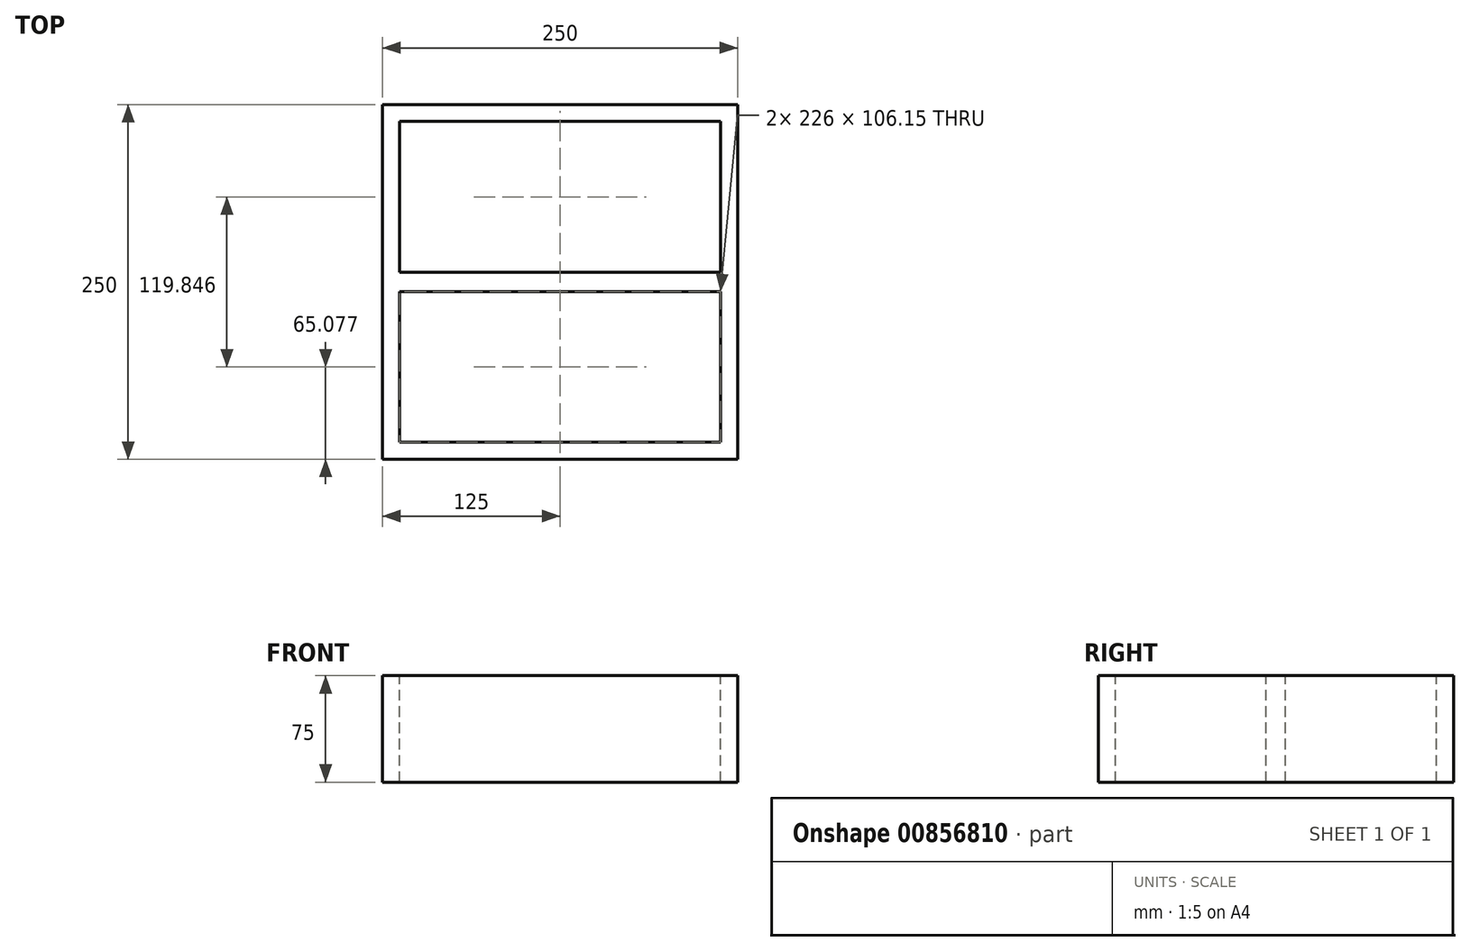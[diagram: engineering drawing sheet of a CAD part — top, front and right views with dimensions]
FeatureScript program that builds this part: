
annotation { "Feature Type Name" : "Feature", "Feature Type Description" : "" }
export const myFeature = defineFeature(function(context is Context, id is Id, definition is map)
    precondition{}
    {
        {
            var Q0;
            Q0=qCreatedBy(makeId("Top.planeOp"),FACE);
            var sketch = newSketch(context, id + "F0", { "sketchPlane" : qUnion([Q0])});
            skLineSegment(sketch, "E0.bottom", {"start": v(-125, 125) * mm, "end": v(125, 125) * mm});
            skLineSegment(sketch, "E0.top", {"start": v(-125, -125) * mm, "end": v(125, -125) * mm});
            skLineSegment(sketch, "E0.left", {"start": v(-125, 125) * mm, "end": v(-125, -125) * mm});
            skLineSegment(sketch, "E0.right", {"start": v(125, 125) * mm, "end": v(125, -125) * mm});
            skPoint(sketch, "E0.middle", {"position": v(0, 0) * mm});
            skSolve(sketch);
        }
        {
            var Q0;
            Q0=makeQuery(id+"F0.imprint","IMPRINT",FACE,{"disambiguationData":[TD([[makeQuery(id+"F0.imprint","IMPRINT",EDGE,{"derivedFrom":sQuery(id+"F0.wireOp",EDGE,"E0.bottom")}),-1.0]])]});
            extrude(context, id + "F1", {"entities" : qUnion([Q0]), "depth" : 75 * mm, "offsetDistance" : 25.4 * mm});
        }
        {
            var Q0;
            Q0=makeQuery(id+"F1.opExtrude","CAP_FACE",FACE,{"disambiguationData":[OSD([sQuery(id+"F0.wireOp",EDGE,"E0.bottom"),sQuery(id+"F0.wireOp",EDGE,"E0.top"),sQuery(id+"F0.wireOp",EDGE,"E0.left"),sQuery(id+"F0.wireOp",EDGE,"E0.right")])],"isStart":false});
            var sketch = newSketch(context, id + "F2", { "sketchPlane" : qUnion([Q0])});
            skLineSegment(sketch, "E1.bottom", {"start": v(-113, 113) * mm, "end": v(113, 113) * mm});
            skLineSegment(sketch, "E1.top", {"start": v(-113, -113) * mm, "end": v(113, -113) * mm});
            skLineSegment(sketch, "E1.left", {"start": v(-113, 113) * mm, "end": v(-113, -113) * mm});
            skLineSegment(sketch, "E1.right", {"start": v(113, 113) * mm, "end": v(113, -113) * mm});
            skPoint(sketch, "E1.middle", {"position": v(0, 0) * mm});
            skSolve(sketch);
        }
        {
            var Q0;
            Q0=makeQuery(id+"F2.imprint","IMPRINT",FACE,{"disambiguationData":[TD([[makeQuery(id+"F2.imprint","IMPRINT",EDGE,{"derivedFrom":sQuery(id+"F2.wireOp",EDGE,"E1.bottom")}),-1.0]])]});
            extrude(context, id + "F3", {"entities" : qUnion([Q0]), "operationType" : NewBodyOperationType.REMOVE, "oppositeDirection" : true, "depth" : 101.6 * mm, "offsetDistance" : 25.4 * mm});
        }
        {
            var Q0;
            Q0=makeQuery(id+"F1.opExtrude","CAP_FACE",FACE,{"disambiguationData":[OSD([sQuery(id+"F0.wireOp",EDGE,"E0.bottom"),sQuery(id+"F0.wireOp",EDGE,"E0.top"),sQuery(id+"F0.wireOp",EDGE,"E0.left"),sQuery(id+"F0.wireOp",EDGE,"E0.right")])],"isStart":false});
            var sketch = newSketch(context, id + "F4", { "sketchPlane" : qUnion([Q0])});
            skLineSegment(sketch, "E2.bottom", {"start": v(-113, 6.85) * mm, "end": v(113, 6.85) * mm});
            skLineSegment(sketch, "E2.top", {"start": v(-113, -6.85) * mm, "end": v(113, -6.85) * mm});
            skLineSegment(sketch, "E2.left", {"start": v(-113, 6.85) * mm, "end": v(-113, -6.85) * mm});
            skLineSegment(sketch, "E2.right", {"start": v(113, 6.85) * mm, "end": v(113, -6.85) * mm});
            skPoint(sketch, "E2.middle", {"position": v(0, 0) * mm});
            skSolve(sketch);
        }
        {
            var Q0;
            Q0=makeQuery(id+"F4.imprint","IMPRINT",FACE,{"disambiguationData":[TD([[makeQuery(id+"F4.imprint","IMPRINT",EDGE,{"derivedFrom":sQuery(id+"F4.wireOp",EDGE,"E2.bottom")}),-1.0]])]});
            extrude(context, id + "F5", {"entities" : qUnion([Q0]), "operationType" : NewBodyOperationType.ADD, "oppositeDirection" : true, "depth" : 75 * mm, "offsetDistance" : 25.4 * mm});
        }
    });
